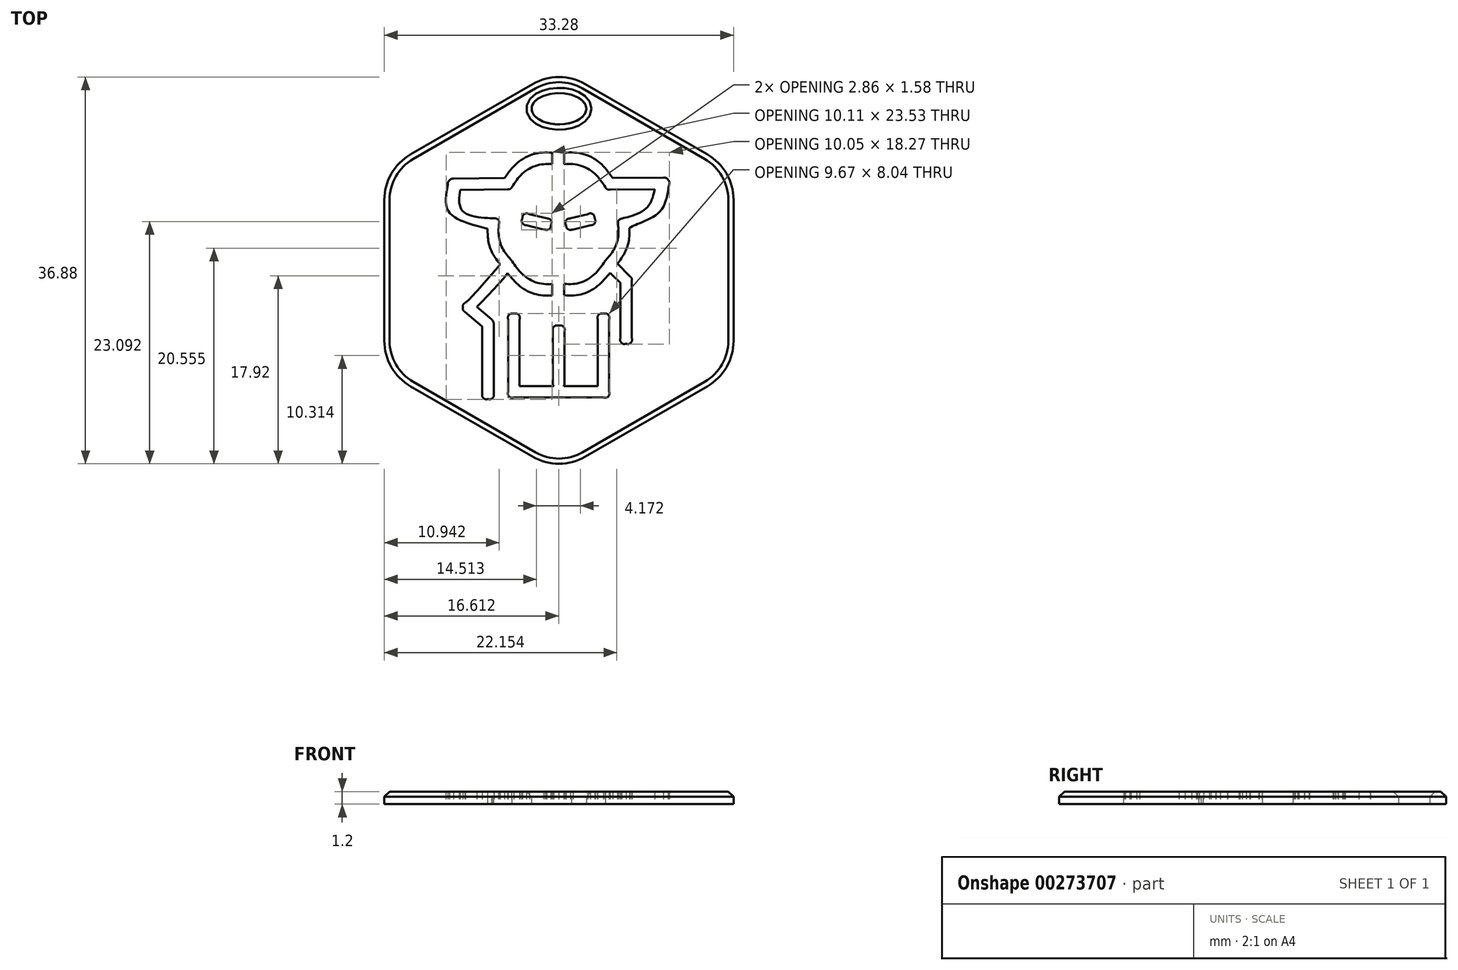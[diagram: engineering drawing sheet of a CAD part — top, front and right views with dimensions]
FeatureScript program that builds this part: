
annotation { "Feature Type Name" : "Feature", "Feature Type Description" : "" }
export const myFeature = defineFeature(function(context is Context, id is Id, definition is map)
    precondition{}
    {
        {
            var Q0;
            Q0=qCreatedBy(makeId("Top.planeOp"),FACE);
            var sketch = newSketch(context, id + "F0", { "sketchPlane" : qUnion([Q0])});
            skCircle(sketch, "E0.cCircle", {"center": v(0, 0) * mm, "radius": 16.64 * mm, "construction": true});
            skLineSegment(sketch, "E0.0", {"start": v(16.64, 6.72) * mm, "end": v(16.64, -6.72) * mm});
            skLineSegment(sketch, "E0.1", {"start": v(14.14, -11.05) * mm, "end": v(2.5, -17.77) * mm});
            skLineSegment(sketch, "E0.2", {"start": v(-2.5, -17.77) * mm, "end": v(-14.14, -11.05) * mm});
            skLineSegment(sketch, "E0.3", {"start": v(-16.64, -6.72) * mm, "end": v(-16.64, 6.72) * mm});
            skLineSegment(sketch, "E0.4", {"start": v(-14.14, 11.05) * mm, "end": v(-2.5, 17.77) * mm});
            skLineSegment(sketch, "E0.5", {"start": v(2.5, 17.77) * mm, "end": v(14.14, 11.05) * mm});
            skPoint(sketch, "E0.0.midPoint", {"position": v(16.64, 0) * mm});
            skPoint(sketch, "E1.visualSharp", {"position": v(-16.64, 9.6) * mm});
            skArc(sketch, "E1.filletArc", {"start": v(-14.14, 11.05) * mm, "mid": v(-15.97, 9.22) * mm, "end": v(-16.64, 6.72) * mm});
            skPoint(sketch, "E2.visualSharp", {"position": v(0, 19.22) * mm});
            skArc(sketch, "E2.filletArc", {"start": v(2.5, 17.77) * mm, "mid": v(0, 18.44) * mm, "end": v(-2.5, 17.77) * mm});
            skPoint(sketch, "E3.visualSharp", {"position": v(16.64, 9.6) * mm});
            skArc(sketch, "E3.filletArc", {"start": v(16.64, 6.72) * mm, "mid": v(15.97, 9.22) * mm, "end": v(14.14, 11.05) * mm});
            skPoint(sketch, "E4.visualSharp", {"position": v(16.64, -9.6) * mm});
            skArc(sketch, "E4.filletArc", {"start": v(14.14, -11.05) * mm, "mid": v(15.97, -9.22) * mm, "end": v(16.64, -6.72) * mm});
            skPoint(sketch, "E5.visualSharp", {"position": v(0, -19.22) * mm});
            skArc(sketch, "E5.filletArc", {"start": v(-2.5, -17.77) * mm, "mid": v(0, -18.44) * mm, "end": v(2.5, -17.77) * mm});
            skPoint(sketch, "E6.visualSharp", {"position": v(-16.64, -9.6) * mm});
            skArc(sketch, "E6.filletArc", {"start": v(-16.64, -6.72) * mm, "mid": v(-15.97, -9.22) * mm, "end": v(-14.14, -11.05) * mm});
            skPoint(sketch, "E7.visualSharp", {"position": v(-14.64, 8.45) * mm});
            skPoint(sketch, "E8.visualSharp", {"position": v(0, 16.9) * mm});
            skPoint(sketch, "E9.visualSharp", {"position": v(14.64, 8.45) * mm});
            skPoint(sketch, "E10.visualSharp", {"position": v(14.64, -8.45) * mm});
            skPoint(sketch, "E11.visualSharp", {"position": v(0, -16.9) * mm});
            skPoint(sketch, "E12.visualSharp", {"position": v(-14.64, -8.45) * mm});
            skEllipse(sketch, "E13", {"center": v(0, 15.41) * mm, "majorRadius": 2.6 * mm, "minorRadius": 1.5 * mm, "majorAxis": v(1, 0)});
            skFitSpline(sketch, "E14", {"points": [v(-6.77, -12.27) * mm, v(-7.07, -12.27) * mm, v(-7.31, -12.02) * mm, v(-7.31, -11.72) * mm]});
            skFitSpline(sketch, "E15", {"points": [v(-8.97, -3.95) * mm, v(-9.1, -3.84) * mm, v(-9.17, -3.67) * mm, v(-9.16, -3.5) * mm]});
            skFitSpline(sketch, "E16", {"points": [v(-9.16, -3.5) * mm, v(-9.15, -3.33) * mm, v(-9.06, -3.17) * mm, v(-8.92, -3.08) * mm]});
            skFitSpline(sketch, "E17", {"points": [v(-8.92, -3.08) * mm, v(-8.66, -2.87) * mm, v(-6.36, -0.31) * mm, v(-5.6, 0.58) * mm]});
            skFitSpline(sketch, "E18", {"points": [v(-5.6, 0.58) * mm, v(-6.29, 1.55) * mm, v(-6.72, 2.72) * mm, v(-6.8, 3.98) * mm]});
            skFitSpline(sketch, "E19", {"points": [v(-6.8, 3.98) * mm, v(-8.28, 4.38) * mm, v(-10.51, 5.62) * mm, v(-10.6, 8.18) * mm]});
            skFitSpline(sketch, "E20", {"points": [v(-10.6, 8.18) * mm, v(-10.6, 8.33) * mm, v(-10.54, 8.47) * mm, v(-10.44, 8.58) * mm]});
            skFitSpline(sketch, "E21", {"points": [v(-10.44, 8.58) * mm, v(-10.34, 8.68) * mm, v(-10.2, 8.74) * mm, v(-10.05, 8.75) * mm]});
            skLineSegment(sketch, "E22", {"start": v(-7.31, -11.72) * mm, "end": v(-7.31, -5.36) * mm});
            skLineSegment(sketch, "E23", {"start": v(-7.31, -5.36) * mm, "end": v(-8.97, -3.95) * mm});
            skFitSpline(sketch, "E24", {"points": [v(-5.18, 8.82) * mm, v(-3.89, 10.32) * mm, v(-2.03, 11.18) * mm, v(-0.04, 11.18) * mm]});
            skFitSpline(sketch, "E25", {"points": [v(-0.04, 11.18) * mm, v(1.96, 11.18) * mm, v(3.83, 10.31) * mm, v(5.12, 8.8) * mm]});
            skLineSegment(sketch, "E26", {"start": v(-10.05, 8.75) * mm, "end": v(-5.18, 8.82) * mm});
            skFitSpline(sketch, "E27", {"points": [v(9.95, 8.85) * mm, v(10.13, 8.84) * mm, v(10.3, 8.77) * mm, v(10.4, 8.62) * mm]});
            skFitSpline(sketch, "E28", {"points": [v(10.4, 8.62) * mm, v(10.5, 8.48) * mm, v(10.53, 8.3) * mm, v(10.48, 8.13) * mm]});
            skFitSpline(sketch, "E29", {"points": [v(10.48, 8.13) * mm, v(9.65, 5.65) * mm, v(7.56, 4.45) * mm, v(6.72, 4.06) * mm]});
            skFitSpline(sketch, "E30", {"points": [v(6.72, 4.06) * mm, v(6.65, 2.8) * mm, v(6.24, 1.62) * mm, v(5.56, 0.64) * mm]});
            skLineSegment(sketch, "E31", {"start": v(5.12, 8.8) * mm, "end": v(9.95, 8.85) * mm});
            skFitSpline(sketch, "E32", {"points": [v(6.79, -0.58) * mm, v(6.89, -0.68) * mm, v(6.95, -0.82) * mm, v(6.95, -0.97) * mm]});
            skLineSegment(sketch, "E33", {"start": v(5.56, 0.64) * mm, "end": v(6.79, -0.58) * mm});
            skFitSpline(sketch, "E34", {"points": [v(6.95, -6.45) * mm, v(6.95, -6.75) * mm, v(6.7, -7) * mm, v(6.4, -7) * mm]});
            skFitSpline(sketch, "E35", {"points": [v(6.4, -7) * mm, v(6.1, -7) * mm, v(5.85, -6.75) * mm, v(5.85, -6.45) * mm]});
            skLineSegment(sketch, "E36", {"start": v(6.95, -0.97) * mm, "end": v(6.95, -6.45) * mm});
            skFitSpline(sketch, "E37", {"points": [v(4.87, -0.22) * mm, v(3.64, -1.52) * mm, v(1.9, -2.33) * mm, v(-0.04, -2.33) * mm]});
            skFitSpline(sketch, "E38", {"points": [v(-0.04, -2.33) * mm, v(-1.95, -2.33) * mm, v(-3.67, -1.54) * mm, v(-4.9, -0.28) * mm]});
            skFitSpline(sketch, "E39", {"points": [v(-4.9, -0.28) * mm, v(-5.67, -1.2) * mm, v(-7.08, -2.7) * mm, v(-7.82, -3.49) * mm]});
            skLineSegment(sketch, "E40", {"start": v(5.85, -6.45) * mm, "end": v(5.85, -1.2) * mm});
            skLineSegment(sketch, "E41", {"start": v(5.85, -1.2) * mm, "end": v(4.87, -0.22) * mm});
            skFitSpline(sketch, "E42", {"points": [v(-6.41, -4.69) * mm, v(-6.4, -4.7) * mm, v(-6.4, -4.7) * mm, v(-6.4, -4.7) * mm]});
            skFitSpline(sketch, "E43", {"points": [v(-6.4, -4.7) * mm, v(-6.34, -4.75) * mm, v(-6.3, -4.81) * mm, v(-6.27, -4.88) * mm]});
            skFitSpline(sketch, "E44", {"points": [v(-6.27, -4.88) * mm, v(-6.24, -4.94) * mm, v(-6.22, -5.01) * mm, v(-6.22, -5.09) * mm]});
            skFitSpline(sketch, "E45", {"points": [v(-6.22, -5.09) * mm, v(-6.22, -5.1) * mm, v(-6.22, -5.1) * mm, v(-6.22, -5.11) * mm]});
            skLineSegment(sketch, "E46", {"start": v(-7.82, -3.49) * mm, "end": v(-6.41, -4.69) * mm});
            skFitSpline(sketch, "E47", {"points": [v(-6.22, -11.72) * mm, v(-6.22, -12.02) * mm, v(-6.46, -12.27) * mm, v(-6.77, -12.27) * mm]});
            skFitSpline(sketch, "E48", {"points": [v(-4.47, 0.88) * mm, v(-3.42, -0.4) * mm, v(-1.83, -1.24) * mm, v(-0.04, -1.24) * mm]});
            skFitSpline(sketch, "E49", {"points": [v(-0.04, -1.24) * mm, v(1.74, -1.24) * mm, v(3.34, -0.4) * mm, v(4.38, 0.88) * mm]});
            skFitSpline(sketch, "E50", {"points": [v(4.38, 0.88) * mm, v(4.4, 0.91) * mm, v(4.42, 0.94) * mm, v(4.45, 0.96) * mm]});
            skFitSpline(sketch, "E51", {"points": [v(4.45, 0.96) * mm, v(5.2, 1.92) * mm, v(5.63, 3.12) * mm, v(5.63, 4.42) * mm]});
            skFitSpline(sketch, "E52", {"points": [v(5.63, 4.42) * mm, v(5.63, 4.65) * mm, v(5.78, 4.86) * mm, v(6, 4.94) * mm]});
            skFitSpline(sketch, "E53", {"points": [v(6, 4.94) * mm, v(6.02, 4.95) * mm, v(8.09, 5.73) * mm, v(9.13, 7.74) * mm]});
            skLineSegment(sketch, "E54", {"start": v(-6.22, -5.11) * mm, "end": v(-6.22, -11.72) * mm});
            skFitSpline(sketch, "E55", {"points": [v(4.87, 7.7) * mm, v(4.7, 7.7) * mm, v(4.54, 7.78) * mm, v(4.43, 7.9) * mm]});
            skFitSpline(sketch, "E56", {"points": [v(4.43, 7.9) * mm, v(3.35, 9.29) * mm, v(1.72, 10.08) * mm, v(-0.04, 10.08) * mm]});
            skFitSpline(sketch, "E57", {"points": [v(-0.04, 10.08) * mm, v(-1.78, 10.08) * mm, v(-3.4, 9.3) * mm, v(-4.49, 7.94) * mm]});
            skFitSpline(sketch, "E58", {"points": [v(-4.49, 7.94) * mm, v(-4.6, 7.81) * mm, v(-4.75, 7.73) * mm, v(-4.9, 7.73) * mm]});
            skLineSegment(sketch, "E59", {"start": v(9.13, 7.74) * mm, "end": v(4.87, 7.7) * mm});
            skFitSpline(sketch, "E60", {"points": [v(-9.43, 7.66) * mm, v(-8.96, 5.47) * mm, v(-6.2, 4.97) * mm, v(-6.17, 4.96) * mm]});
            skFitSpline(sketch, "E61", {"points": [v(-6.17, 4.96) * mm, v(-5.9, 4.92) * mm, v(-5.72, 4.69) * mm, v(-5.72, 4.42) * mm]});
            skFitSpline(sketch, "E62", {"points": [v(-5.72, 4.42) * mm, v(-5.72, 3.11) * mm, v(-5.27, 1.9) * mm, v(-4.52, 0.95) * mm]});
            skFitSpline(sketch, "E63", {"points": [v(-4.52, 0.95) * mm, v(-4.5, 0.93) * mm, v(-4.49, 0.91) * mm, v(-4.48, 0.9) * mm]});
            skFitSpline(sketch, "E64", {"points": [v(-4.48, 0.9) * mm, v(-4.47, 0.9) * mm, v(-4.47, 0.89) * mm, v(-4.46, 0.88) * mm]});
            skLineSegment(sketch, "E65", {"start": v(-4.9, 7.73) * mm, "end": v(-9.43, 7.66) * mm});
            skFitSpline(sketch, "E66", {"points": [v(-4.3, -12.13) * mm, v(-4.6, -12.13) * mm, v(-4.85, -11.88) * mm, v(-4.85, -11.58) * mm]});
            skLineSegment(sketch, "E67", {"start": v(4.24, -12.13) * mm, "end": v(-4.3, -12.13) * mm});
            skFitSpline(sketch, "E68", {"points": [v(-4.85, -4.67) * mm, v(-4.85, -4.37) * mm, v(-4.6, -4.13) * mm, v(-4.3, -4.13) * mm]});
            skFitSpline(sketch, "E69", {"points": [v(-4.3, -4.13) * mm, v(-4, -4.13) * mm, v(-3.75, -4.37) * mm, v(-3.75, -4.67) * mm]});
            skLineSegment(sketch, "E70", {"start": v(-4.85, -11.58) * mm, "end": v(-4.85, -4.67) * mm});
            skFitSpline(sketch, "E71", {"points": [v(-0.5, -11.03) * mm, v(-0.55, -10.95) * mm, v(-0.58, -10.85) * mm, v(-0.58, -10.75) * mm]});
            skLineSegment(sketch, "E72", {"start": v(-3.75, -4.67) * mm, "end": v(-3.75, -11.03) * mm});
            skLineSegment(sketch, "E73", {"start": v(-3.75, -11.03) * mm, "end": v(-0.5, -11.03) * mm});
            skFitSpline(sketch, "E74", {"points": [v(-0.58, -5.81) * mm, v(-0.58, -5.51) * mm, v(-0.33, -5.27) * mm, v(-0.03, -5.27) * mm]});
            skFitSpline(sketch, "E75", {"points": [v(-0.03, -5.27) * mm, v(0.27, -5.27) * mm, v(0.52, -5.51) * mm, v(0.52, -5.81) * mm]});
            skLineSegment(sketch, "E76", {"start": v(-0.58, -10.75) * mm, "end": v(-0.58, -5.81) * mm});
            skFitSpline(sketch, "E77", {"points": [v(0.52, -10.75) * mm, v(0.52, -10.85) * mm, v(0.5, -10.95) * mm, v(0.45, -11.03) * mm]});
            skLineSegment(sketch, "E78", {"start": v(0.52, -5.81) * mm, "end": v(0.52, -10.75) * mm});
            skFitSpline(sketch, "E79", {"points": [v(3.7, -4.67) * mm, v(3.7, -4.37) * mm, v(3.94, -4.13) * mm, v(4.24, -4.13) * mm]});
            skFitSpline(sketch, "E80", {"points": [v(4.24, -4.13) * mm, v(4.54, -4.13) * mm, v(4.8, -4.37) * mm, v(4.8, -4.67) * mm]});
            skLineSegment(sketch, "E81", {"start": v(0.45, -11.03) * mm, "end": v(3.7, -11.03) * mm});
            skLineSegment(sketch, "E82", {"start": v(3.7, -11.03) * mm, "end": v(3.7, -4.67) * mm});
            skFitSpline(sketch, "E83", {"points": [v(4.8, -11.58) * mm, v(4.8, -11.88) * mm, v(4.54, -12.13) * mm, v(4.24, -12.13) * mm]});
            skFitSpline(sketch, "E84", {"points": [v(-1.3, 3.87) * mm, v(-1.34, 3.87) * mm, v(-1.39, 3.88) * mm, v(-1.43, 3.9) * mm]});
            skLineSegment(sketch, "E85", {"start": v(4.8, -4.67) * mm, "end": v(4.8, -11.58) * mm});
            skFitSpline(sketch, "E86", {"points": [v(-3.09, 4.3) * mm, v(-3.38, 4.38) * mm, v(-3.56, 4.67) * mm, v(-3.49, 4.97) * mm]});
            skFitSpline(sketch, "E87", {"points": [v(-3.49, 4.97) * mm, v(-3.41, 5.26) * mm, v(-3.12, 5.44) * mm, v(-2.82, 5.37) * mm]});
            skLineSegment(sketch, "E88", {"start": v(-1.43, 3.9) * mm, "end": v(-3.09, 4.3) * mm});
            skFitSpline(sketch, "E89", {"points": [v(-1.17, 4.95) * mm, v(-0.87, 4.88) * mm, v(-0.7, 4.58) * mm, v(-0.77, 4.3) * mm]});
            skFitSpline(sketch, "E90", {"points": [v(-0.77, 4.3) * mm, v(-0.83, 4.04) * mm, v(-1.05, 3.87) * mm, v(-1.3, 3.87) * mm]});
            skFitSpline(sketch, "E91", {"points": [v(1.22, 3.87) * mm, v(0.97, 3.87) * mm, v(0.75, 4.04) * mm, v(0.69, 4.3) * mm]});
            skFitSpline(sketch, "E92", {"points": [v(0.69, 4.3) * mm, v(0.61, 4.58) * mm, v(0.8, 4.88) * mm, v(1.09, 4.95) * mm]});
            skLineSegment(sketch, "E93", {"start": v(-2.82, 5.37) * mm, "end": v(-1.17, 4.95) * mm});
            skFitSpline(sketch, "E94", {"points": [v(2.74, 5.37) * mm, v(3.03, 5.44) * mm, v(3.33, 5.26) * mm, v(3.4, 4.97) * mm]});
            skFitSpline(sketch, "E95", {"points": [v(3.4, 4.97) * mm, v(3.48, 4.67) * mm, v(3.3, 4.38) * mm, v(3, 4.3) * mm]});
            skLineSegment(sketch, "E96", {"start": v(1.09, 4.95) * mm, "end": v(2.74, 5.37) * mm});
            skFitSpline(sketch, "E97", {"points": [v(1.35, 3.9) * mm, v(1.3, 3.88) * mm, v(1.26, 3.87) * mm, v(1.22, 3.87) * mm]});
            skLineSegment(sketch, "E98", {"start": v(3, 4.3) * mm, "end": v(1.35, 3.9) * mm});
            skLineSegment(sketch, "E99.bottom", {"start": v(-0.64, 11.44) * mm, "end": v(0.5, 11.44) * mm});
            skLineSegment(sketch, "E99.top", {"start": v(-0.64, 9.6) * mm, "end": v(0.5, 9.6) * mm});
            skLineSegment(sketch, "E99.left", {"start": v(-0.64, 11.44) * mm, "end": v(-0.64, 9.6) * mm});
            skLineSegment(sketch, "E99.right", {"start": v(0.5, 11.44) * mm, "end": v(0.5, 9.6) * mm});
            skLineSegment(sketch, "E100.bottom", {"start": v(0.5, -2.83) * mm, "end": v(-0.64, -2.83) * mm});
            skLineSegment(sketch, "E100.top", {"start": v(0.5, -0.7) * mm, "end": v(-0.64, -0.7) * mm});
            skLineSegment(sketch, "E100.left", {"start": v(0.5, -2.83) * mm, "end": v(0.5, -0.7) * mm});
            skLineSegment(sketch, "E100.right", {"start": v(-0.64, -2.83) * mm, "end": v(-0.64, -0.7) * mm});
            skSolve(sketch);
        }
        {
            var Q0;
            Q0=qSketchRegion(id+"F0",true);
            var Q1;
            Q1=makeQuery(id+"F0.imprint","IMPRINT",FACE,{"disambiguationData":[TD([[makeQuery(id+"F0.imprint","IMPRINT",EDGE,{"derivedFrom":sQuery(id+"F0.wireOp",EDGE,"E48")}),1.0]])]});
            var Q2;
            {var subQ5=sQuery(id+"F0.wireOp",EDGE,"E25");var subQ6=sQuery(id+"F0.wireOp",EDGE,"E24");var subQ7=makeQuery(id+"F0.imprint","INTERSECT",VERTEX,{"derivedFrom":[subQ6,subQ5]});Q2=makeQuery(id+"F0.imprint","IMPRINT",FACE,{"disambiguationData":[TD([[makeQuery(id+"F0.imprint","IMPRINT",EDGE,{"disambiguationData":[TD([[subQ7,1.0]])],"derivedFrom":subQ6}),-1.0]])]});}
            var Q3;
            {var subQ0=sQuery(id+"F0.wireOp",EDGE,"E99.bottom");Q3=makeQuery(id+"F0.imprint","IMPRINT",FACE,{"disambiguationData":[TD([[makeQuery(id+"F0.imprint","IMPRINT",EDGE,{"derivedFrom":subQ0}),-1.0]])]});}
            var Q4;
            {var subQ1=sQuery(id+"F0.wireOp",EDGE,"E99.top");Q4=makeQuery(id+"F0.imprint","IMPRINT",FACE,{"disambiguationData":[TD([[makeQuery(id+"F0.imprint","IMPRINT",EDGE,{"derivedFrom":subQ1}),1.0]])]});}
            var Q5;
            {var subQ7=sQuery(id+"F0.wireOp",EDGE,"E38");var subQ8=sQuery(id+"F0.wireOp",EDGE,"E37");var subQ9=makeQuery(id+"F0.imprint","INTERSECT",VERTEX,{"derivedFrom":[subQ8,subQ7]});Q5=makeQuery(id+"F0.imprint","IMPRINT",FACE,{"disambiguationData":[TD([[makeQuery(id+"F0.imprint","IMPRINT",EDGE,{"disambiguationData":[TD([[subQ9,1.0]])],"derivedFrom":subQ8}),-1.0]])]});}
            var Q6;
            {var subQ1=sQuery(id+"F0.wireOp",EDGE,"E100.bottom");Q6=makeQuery(id+"F0.imprint","IMPRINT",FACE,{"disambiguationData":[TD([[makeQuery(id+"F0.imprint","IMPRINT",EDGE,{"derivedFrom":subQ1}),-1.0]])]});}
            var Q7;
            {var subQ9=sQuery(id+"F0.wireOp",EDGE,"E50");Q7=makeQuery(id+"F0.imprint","IMPRINT",FACE,{"disambiguationData":[TD([[makeQuery(id+"F0.imprint","IMPRINT",EDGE,{"derivedFrom":subQ9}),1.0]])]});}
            extrude(context, id + "F1", {"entities" : qUnion([Q0, Q1, Q2, Q3, Q4, Q5, Q6, Q7]), "depth" : 1.2 * mm});
        }
        {
            var Q0;
            Q0=makeQuery(id+"F1.opExtrude","CAP_EDGE",EDGE,{"disambiguationData":[OSD([sQuery(id+"F0.wireOp",EDGE,"E0.2")])],"isStart":false});
            chamfer(context, id + "F2", {"entities" : qUnion([Q0]), "width" : 0.5 * mm, "tangentPropagation" : true});
        }
        {
            var Q0;
            Q0=makeQuery(id+"F1.opExtrude","CAP_EDGE",EDGE,{"disambiguationData":[OSD([sQuery(id+"F0.wireOp",EDGE,"E13")])],"isStart":false});
            chamfer(context, id + "F3", {"entities" : qUnion([Q0]), "width" : 0.5 * mm, "tangentPropagation" : true});
        }
    });
